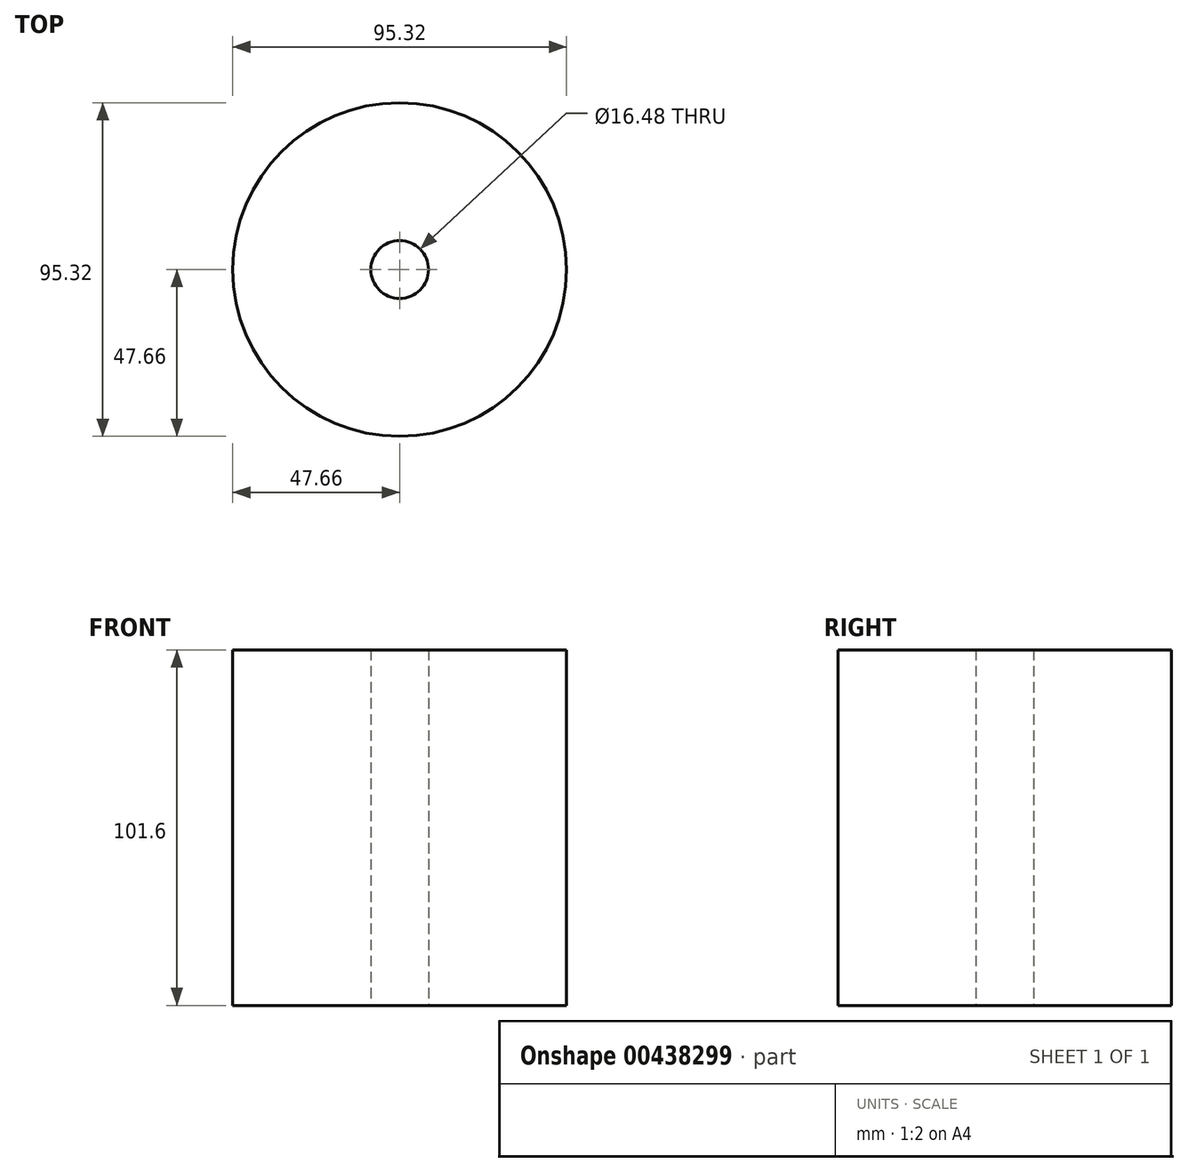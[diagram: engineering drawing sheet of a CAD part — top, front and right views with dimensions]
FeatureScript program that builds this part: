
annotation { "Feature Type Name" : "Feature", "Feature Type Description" : "" }
export const myFeature = defineFeature(function(context is Context, id is Id, definition is map)
    precondition{}
    {
        {
            var Q0;
            Q0=qCreatedBy(makeId("Top.planeOp"),FACE);
            var sketch = newSketch(context, id + "F0", { "sketchPlane" : qUnion([Q0])});
            skCircle(sketch, "E0", {"center": v(0, 0) * mm, "radius": 47.66 * mm});
            skSolve(sketch);
        }
        {
            var Q0;
            Q0=makeQuery(id+"F0.imprint","IMPRINT",FACE,{"disambiguationData":[TD([[makeQuery(id+"F0.imprint","IMPRINT",EDGE,{"derivedFrom":sQuery(id+"F0.wireOp",EDGE,"E0")}),1.0]])]});
            var sketch = newSketch(context, id + "F1", { "sketchPlane" : qUnion([Q0])});
            skCircle(sketch, "E1", {"center": v(0, 0) * mm, "radius": 13.04 * mm});
            skSolve(sketch);
        }
        {
            var Q0;
            Q0=makeQuery(id+"F0.imprint","IMPRINT",FACE,{"disambiguationData":[TD([[makeQuery(id+"F0.imprint","IMPRINT",EDGE,{"derivedFrom":sQuery(id+"F0.wireOp",EDGE,"E0")}),1.0]])]});
            extrude(context, id + "F2", {"entities" : qUnion([Q0]), "depth" : 101.6 * mm});
        }
        {
            var Q0;
            Q0=makeQuery(id+"F1.imprint","IMPRINT",FACE,{"disambiguationData":[TD([[makeQuery(id+"F1.imprint","IMPRINT",EDGE,{"derivedFrom":sQuery(id+"F1.wireOp",EDGE,"E1")}),1.0]])]});
            extrude(context, id + "F3", {"entities" : qUnion([Q0]), "operationType" : NewBodyOperationType.ADD, "depth" : 101.6 * mm});
        }
        {
            var Q0;
            Q0=makeQuery(id+"F2.opExtrude","CAP_FACE",FACE,{"disambiguationData":[OSD([sQuery(id+"F0.wireOp",EDGE,"E0")])],"isStart":true});
            var sketch = newSketch(context, id + "F4", { "sketchPlane" : qUnion([Q0])});
            skCircle(sketch, "E2", {"center": v(0, 0) * mm, "radius": 8.24 * mm});
            skSolve(sketch);
        }
        {
            var Q0;
            Q0=makeQuery(id+"F4.imprint","IMPRINT",FACE,{"disambiguationData":[TD([[makeQuery(id+"F4.imprint","IMPRINT",EDGE,{"derivedFrom":sQuery(id+"F4.wireOp",EDGE,"E2")}),1.0]])]});
            extrude(context, id + "F5", {"entities" : qUnion([Q0]), "operationType" : NewBodyOperationType.REMOVE, "oppositeDirection" : true, "depth" : 101.6 * mm});
        }
    });
